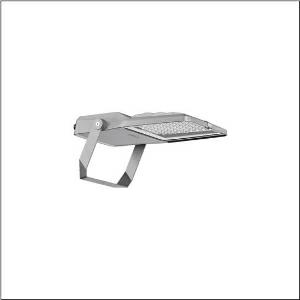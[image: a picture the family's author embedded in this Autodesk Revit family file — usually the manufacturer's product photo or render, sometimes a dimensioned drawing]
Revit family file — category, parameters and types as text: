
# Revit family: floodlight_fl_21_mini___pl33t_5xa7772b3f1a_a1df
name_source: partatom
category: Lighting Fixtures
units: mm (PartAtom-declared; Revit-internal decimal feet)

## family parameters
Cut with Voids When Loaded = No
Host = Face
Light Source = No
Part Type = Normal
Room Calculation Point = No
Round Connector Dimension = Use Diameter
Shared = No

## types (1)
- --- (1 x LED, 5310 lm, 45.5 W, 3000K)
    Apparent Load = 46 VA
    CIE Flux Codes = 26 75 99 100 100
    Color Rendering = 80
    Color Temperature = 3000K
    Default Elevation = 1800 mm
    Description = Floodlight FL 21 mini, floodlight, primary light control with lens, of PMMA, primary optical cover: protective disc, of toughened safety glass, transparent, light distribution: PL33T, light emission: direct distribution, installation type: surface-mounted, LED, High Power LED, rated luminous flux: 5.310lm, luminous efficacy: 117lm/W, light colour: 830, colour temperature: 3000K, control gear: ECG iQ, control: Street-Remote, Auto-Match, Temp-Guard, Night-Set, Smart-Wire, Desk-Remote (wireless, voltage-free reading and setting of iQ features in the workshop via application-optimized NFC function/RFID function), optimised constant luminous flux control (CLO 2.0), with terminal, 6-pole, mains connection: 220..240V, AC, 50/60Hz, start of lifetime: 46W, end of lifetime: 48W, reduction: 21W, luminaire housing, of diecast aluminium, powder-coated, Siteco® metallic grey (DB 702S), corrosivity category C5 according to DIN EN ISO 12944, mounting bracket, of steel, galvanised, powder-coated, Siteco® metallic grey (DB 702S), protection rating (complete): IP66, insulation class (complete): insulation class II (safety insulation), certification: CE, ENEC, VDE, protection symbol: D, impact resistance: IK08, permissible operating ambient temperature: -40..+40°C, permissible operating ambient temperature for outdoor applications: -40..+50°C, standard: DIN EN 12944, packaging unit: 1 piece

Light Distribution: PL33T
    Height = 70 mm
    Lamp = 1 x LED
    Lamp Light Flux = 5310 lm
    Lamp Power = 45.5 W
    Lamp count = 1
    Length = 485 mm
    Luminous efficacy = 117 lm/W
    Manufacturer = Siteco
    ModVariant = No
    Model = 5XA7772B3F1A
    Number of Poles = 1
    OnlyDefault = Yes
    Power Factor = 1
    Product Name = Floodlight FL 21 mini | PL33T
    Product group = floodlight | pylon top
    ProductGroupID = 6101
    Protection Class = Protection class II
    Protection Degree = IP 66
    RLX_Detail_Level = 1
    RlxData = <blob elided: 95893 chars, md5=32d7b604>
    Socket = socket
    Standby Power = 0 W
    System Light Flux = 5310 lm
    System Power = 46 W
    Type Comments = factory setting: luminous flux: 100 % | dim-lin: 254 | 463 mA
    Type Image = l_1006845.jpg
    URL = http://relux.com
    VarID = @adj_060017
    Voltage = 0 V
    Weight = 0.00 kg
    Width = 337 mm

## geometry (parser evidence)
native form markers: Blend x4, Sweep x12
no freeform markers — native parametric forms only
